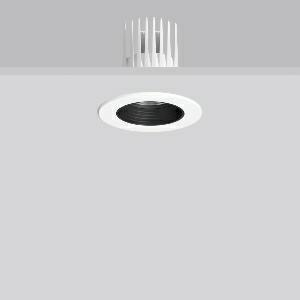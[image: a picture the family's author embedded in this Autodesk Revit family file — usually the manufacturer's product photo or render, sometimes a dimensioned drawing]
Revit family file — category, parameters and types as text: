
# Revit family: heledon_mini_e_901744_002_3_a337
name_source: partatom
category: Lighting Fixtures
units: mm (PartAtom-declared; Revit-internal decimal feet)

## family parameters
Cut with Voids When Loaded = No
Host = Face
Light Source = No
Part Type = Normal
Room Calculation Point = No
Round Connector Dimension = Use Diameter
Shared = No

## types (1)
- HELEDON mini E (1 x LED Modul 935, 2150 lm, 3500)
    Apparent Load = 20 VA
    Approval mark = CE
    CIE Flux Codes = 96 100 100 100 100
    Color Rendering = 92
    Color Temperature = 3500
    Default Elevation = 1800 mm
    Description = Series: HELEDON mini
Round recessed downlight. Housing: die-cast aluminium, powder-coated. Black plastic ring and recessed LED to prevent glare from the side. Optical assembly with lens made of plastic (polycarbonate) for the best homogeneous light distribution - can be changed without tools. Best colour rendering index Ra>90. Suitable for Recessed ceiling mounting. Installation without tools thanks to spring fastening system. Including separate LED converter with connecting cable 600 mm.High quality converter without flickering and stroboscopic effect. Through-wiring box (5 pole) available as accessory. The following accessories can be mounted without use of tools: interchangeable lenses, decorative glasses, honeycomb louvre, clear and frosted diffusers, white interchangeable plastic ring. 
Colour: traffic white, matt (RAL 9016)
Diameter: 124 mm
Height: 3 mm
Cut-out diameter: 114 mm
Recess height: 170 mm
Luminaire: recess height: 120 mm
Lamp: LED
Socket: without socket
Colour temperature: 3500K
Colour rendering index (CRI): 92
System power: 20 W
Rated luminous flux: 2150 lm
Luminous efficiency: 108 lm/W
Control gear: Regulated power supply
Protection class: II
Type of protection: IP 20
    Height = 0 mm  [stored 0 ft]
    Lamp = 1 x LED Modul 935
    Lamp Light Flux = 2150 lm
    Lamp count = 1
    Length = 124 mm  [stored 0.406824 ft]
    Lifetime = 50000 h
    Luminous efficacy = 108 lm/W
    Manufacturer = RZB
    ModVariant = No
    Model = 901744.002.3
    Mounting Place = Ceiling
    Mounting Type = Recessed
    Number of Poles = 1
    OnlyDefault = Yes
    Power Factor = 1
    Product Name = HELEDON mini E
    Product group = Recessed downlights
    ProductGroupID = 402
    Protection Class = Protection class II
    Protection Degree = IP 20
    RLX_Detail_Level = 1
    RLX_Emergency_Light_Flux = 0 lm
    RLX_Emergency_Type = 0
    RLX_Emergency_Type_DB = No
    RlxData = <blob elided: 126753 chars, md5=ba2f6905>
    Socket = socket
    Standby Power = 0 W
    System Light Flux = 2150 lm
    System Power = 20 W
    Type Comments = Product without accessories
    Type Image = 901656.002.jpg
    URL = http://relux.com
    VarID = ---
    Voltage = 230 V
    Voltage Range = 220-240 V
    Weight = 0.00 kg
    Width = 0 mm  [stored 0 ft]

note: [stored X ft] marks values corroborated as IEEE doubles in the binary element streams (Revit-internal decimal feet)

## geometry (parser evidence)
native form markers: Blend x4, Sweep x11
no freeform markers — native parametric forms only
